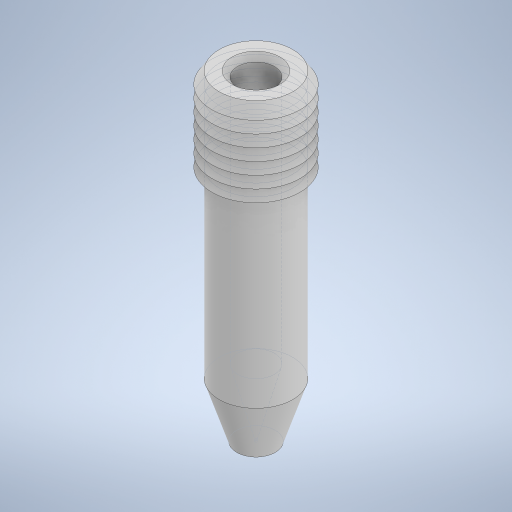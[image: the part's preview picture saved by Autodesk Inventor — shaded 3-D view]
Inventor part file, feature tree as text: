
AUTODESK INVENTOR PART (.ipt)
format: ipt  version: 2024.2 (Build 282272000, 272)  size: 311,808 bytes
history: native  units: mm
features: revolve x1, sketch x1
ambient origin geometry x8: Origin, YZ Plane, XZ Plane, XY Plane, X Axis, Y Axis, Z Axis, Center Point
bodies: Solid1 (feature_tree)
feature tree (2):
  revolve  "Revolution1"  [1 undecoded]
  sketch  "Sketch1"  dims[d3=0.2mm d4=2.0mm d5=50.0mm d7=1.3mm d8=10.0mm d10=10.0mm d12=1.3mm d13=0.0mm d14=0.8mm d15=360.0deg d17=8.0mm d19=0.6mm d20=0.6mm d22=30.0mm d24=1.3mm d25=10.0mm d27=10.0mm d29=20.0mm d30=2.0mm]
note: 1 required parameter value undecoded (feature->parameter linkage not recoverable at this tier; creation-order binding heuristic only, values carry confidence <= 0.55)
